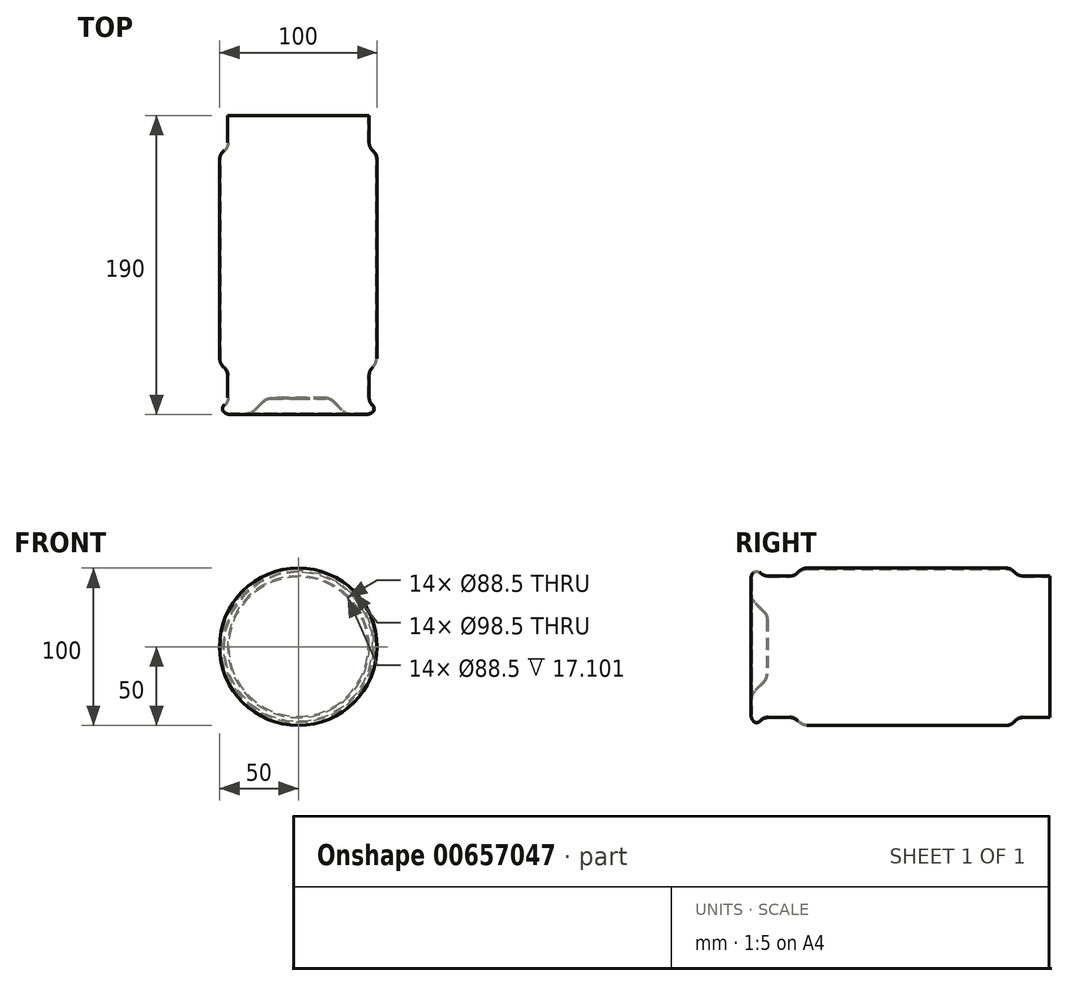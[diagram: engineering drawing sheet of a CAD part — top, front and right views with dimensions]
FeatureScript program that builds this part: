
annotation { "Feature Type Name" : "Feature", "Feature Type Description" : "" }
export const myFeature = defineFeature(function(context is Context, id is Id, definition is map)
    precondition{}
    {
        {
            var Q0;
            Q0=qCreatedBy(makeId("Top.planeOp"),FACE);
            var sketch = newSketch(context, id + "F0", { "sketchPlane" : qUnion([Q0])});
            skLineSegment(sketch, "E0", {"start": v(0, 105) * mm, "end": v(0, -105) * mm});
            skLineSegment(sketch, "E1", {"start": v(-70, 0) * mm, "end": v(70, 0) * mm});
            skLineSegment(sketch, "E2", {"start": v(-32.9, -95) * mm, "end": v(-43, -95) * mm});
            skLineSegment(sketch, "E3", {"start": v(-50, -59.33) * mm, "end": v(-50, 67.1) * mm});
            skLineSegment(sketch, "E4", {"start": v(-47.05, 72.95) * mm, "end": v(-47.95, 72.05) * mm});
            skLineSegment(sketch, "E5", {"start": v(-45, 95) * mm, "end": v(-45, 77.9) * mm});
            skArc(sketch, "E6", {"start": v(-47.95, 72.05) * mm, "mid": v(-49.47, 69.78) * mm, "end": v(-50, 67.1) * mm});
            skArc(sketch, "E7", {"start": v(-47.05, 72.95) * mm, "mid": v(-45.53, 75.22) * mm, "end": v(-45, 77.9) * mm});
            skLineSegment(sketch, "E8", {"start": v(-44.25, 95) * mm, "end": v(-44.25, 77.9) * mm});
            skArc(sketch, "E9", {"start": v(-46.52, 72.42) * mm, "mid": v(-44.84, 74.93) * mm, "end": v(-44.25, 77.9) * mm});
            skArc(sketch, "E10", {"start": v(-47.42, 71.52) * mm, "mid": v(-48.77, 69.5) * mm, "end": v(-49.25, 67.1) * mm});
            skLineSegment(sketch, "E11", {"start": v(-49.25, -59.33) * mm, "end": v(-49.25, 67.1) * mm});
            skLineSegment(sketch, "E12", {"start": v(-46.52, 72.42) * mm, "end": v(-47.42, 71.52) * mm});
            skLineSegment(sketch, "E13", {"start": v(-45, 95) * mm, "end": v(-44.25, 95) * mm});
            skLineSegment(sketch, "E14", {"start": v(0, -85) * mm, "end": v(-17.1, -85) * mm});
            skLineSegment(sketch, "E15", {"start": v(-27.95, -92.95) * mm, "end": v(-22.05, -87.05) * mm});
            skArc(sketch, "E16", {"start": v(-17.1, -85) * mm, "mid": v(-19.78, -85.53) * mm, "end": v(-22.05, -87.05) * mm});
            skArc(sketch, "E17", {"start": v(-32.9, -95) * mm, "mid": v(-30.22, -94.47) * mm, "end": v(-27.95, -92.95) * mm});
            skLineSegment(sketch, "E18", {"start": v(-32.9, -94.25) * mm, "end": v(-43, -94.25) * mm});
            skArc(sketch, "E19", {"start": v(-32.9, -94.25) * mm, "mid": v(-30.5, -93.77) * mm, "end": v(-28.48, -92.42) * mm});
            skLineSegment(sketch, "E20", {"start": v(-28.48, -92.42) * mm, "end": v(-22.58, -86.52) * mm});
            skArc(sketch, "E21", {"start": v(-17.1, -84.25) * mm, "mid": v(-20.07, -84.84) * mm, "end": v(-22.58, -86.52) * mm});
            skLineSegment(sketch, "E22", {"start": v(0, -84.25) * mm, "end": v(-17.1, -84.25) * mm});
            skLineSegment(sketch, "E23", {"start": v(0, -84.25) * mm, "end": v(0, -85) * mm});
            skLineSegment(sketch, "E24", {"start": v(-44.25, -84.25) * mm, "end": v(-44.25, -70.05) * mm});
            skArc(sketch, "E25", {"start": v(-44.25, -70.05) * mm, "mid": v(-44.9, -67.1) * mm, "end": v(-46.75, -64.69) * mm});
            skArc(sketch, "E26", {"start": v(-49.25, -59.33) * mm, "mid": v(-48.6, -62.28) * mm, "end": v(-46.75, -64.69) * mm});
            skArc(sketch, "E27", {"start": v(-50, -59.33) * mm, "mid": v(-49.27, -62.6) * mm, "end": v(-47.23, -65.26) * mm});
            skArc(sketch, "E28", {"start": v(-45, -70.05) * mm, "mid": v(-45.59, -67.4) * mm, "end": v(-47.23, -65.26) * mm});
            skLineSegment(sketch, "E29", {"start": v(-45, -84.25) * mm, "end": v(-45, -70.05) * mm});
            skArc(sketch, "E30", {"start": v(-46.83, -88.67) * mm, "mid": v(-45.48, -86.64) * mm, "end": v(-45, -84.25) * mm});
            skLineSegment(sketch, "E31", {"start": v(-47.36, -89.2) * mm, "end": v(-46.83, -88.67) * mm});
            skArc(sketch, "E32", {"start": v(-46.91, -93.8) * mm, "mid": v(-45.05, -94.7) * mm, "end": v(-43, -95) * mm});
            skArc(sketch, "E33", {"start": v(-47.36, -89.2) * mm, "mid": v(-48.22, -91.6) * mm, "end": v(-46.91, -93.8) * mm});
            skArc(sketch, "E34", {"start": v(-46.3, -89.2) * mm, "mid": v(-44.78, -86.93) * mm, "end": v(-44.25, -84.25) * mm});
            skLineSegment(sketch, "E35", {"start": v(-46.83, -89.73) * mm, "end": v(-46.3, -89.2) * mm});
            skArc(sketch, "E36", {"start": v(-46.83, -89.73) * mm, "mid": v(-47.48, -91.53) * mm, "end": v(-46.5, -93.18) * mm});
            skArc(sketch, "E37", {"start": v(-46.5, -93.18) * mm, "mid": v(-44.83, -93.98) * mm, "end": v(-43, -94.25) * mm});
            skSolve(sketch);
        }
        {
            var Q0;
            Q0=makeQuery(id+"F0.imprint","IMPRINT",FACE,{"disambiguationData":[TD([[makeQuery(id+"F0.imprint","IMPRINT",EDGE,{"derivedFrom":sQuery(id+"F0.wireOp",EDGE,"E4")}),1.0]])]});
            var Q1;
            Q1=makeQuery(id+"F0.imprint","IMPRINT",FACE,{"disambiguationData":[TD([[makeQuery(id+"F0.imprint","IMPRINT",EDGE,{"derivedFrom":sQuery(id+"F0.wireOp",EDGE,"E2")}),-1.0]])]});
            var Q2;
            Q2=sQuery(id+"F0.wireOp",EDGE,"E0");
            revolve(context, id + "F1", {"entities" : qUnion([Q0, Q1]), "axis" : qUnion([Q2]), "revolveType" : RevolveType.FULL});
        }
    });
